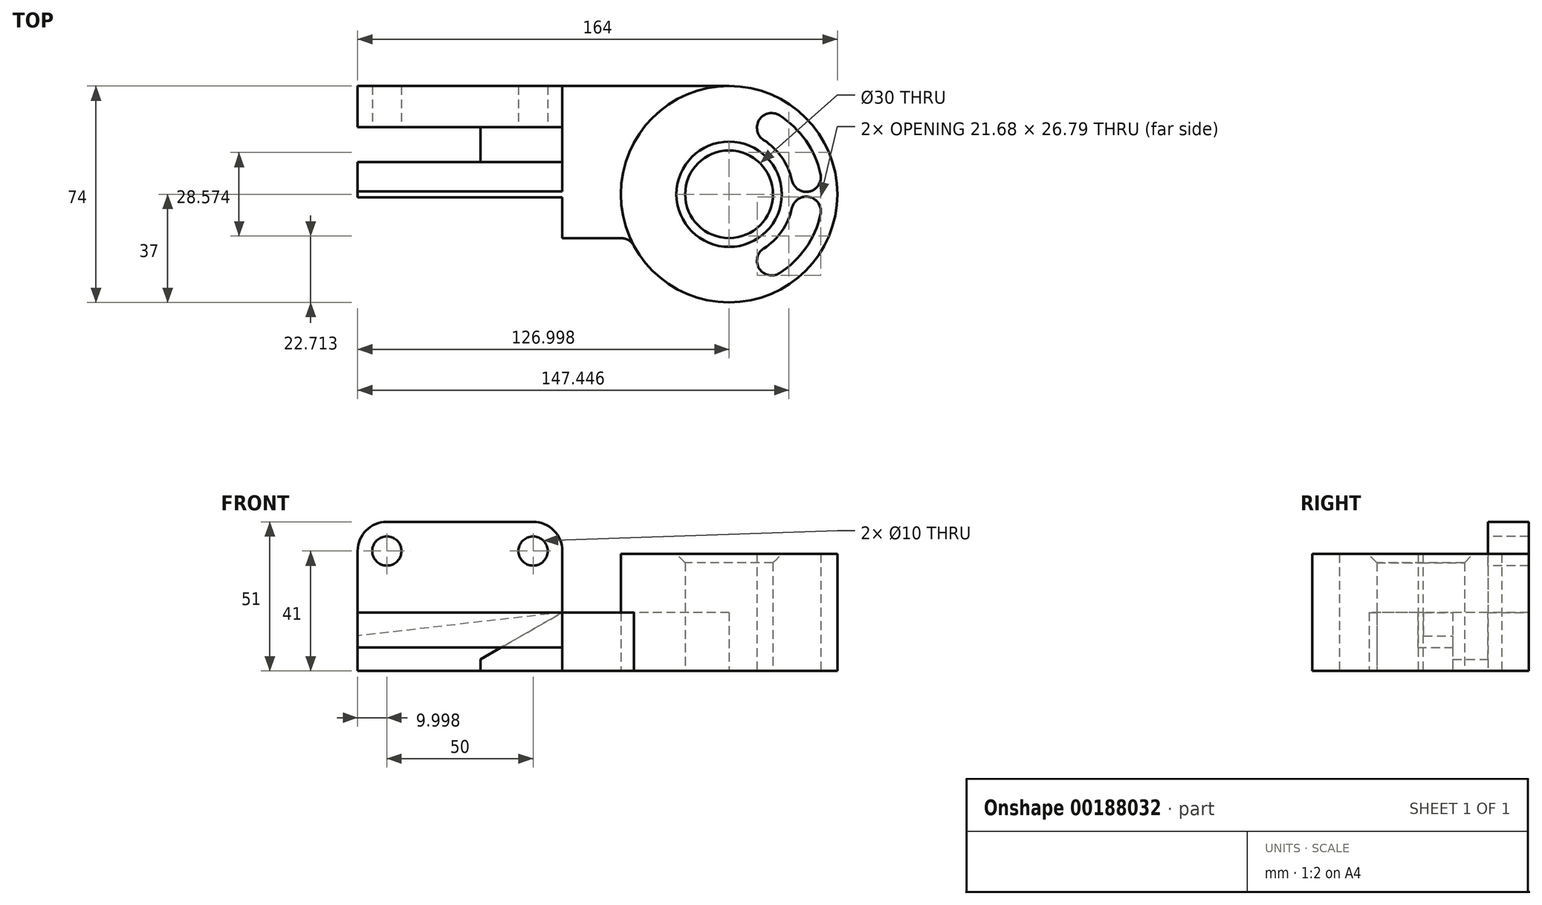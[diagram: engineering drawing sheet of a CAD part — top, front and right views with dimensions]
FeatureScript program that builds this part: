
annotation { "Feature Type Name" : "Feature", "Feature Type Description" : "" }
export const myFeature = defineFeature(function(context is Context, id is Id, definition is map)
    precondition{}
    {
        {
            var Q0;
            Q0=qCreatedBy(makeId("Top.planeOp"),FACE);
            var sketch = newSketch(context, id + "F0", { "sketchPlane" : qUnion([Q0])});
            skCircle(sketch, "E0", {"center": v(50.74, 37) * mm, "radius": 37 * mm});
            skArc(sketch, "E1", {"start": v(67.96, 10.03) * mm, "mid": v(76.97, 18.67) * mm, "end": v(81.99, 30.1) * mm});
            skCircle(sketch, "E2", {"center": v(50.74, 37) * mm, "radius": 22 * mm});
            skCircle(sketch, "E3", {"center": v(50.74, 37) * mm, "radius": 15 * mm});
            skArc(sketch, "E4", {"start": v(81.99, 30.1) * mm, "mid": v(78.18, 36.07) * mm, "end": v(72.22, 32.26) * mm});
            skArc(sketch, "E5", {"start": v(62.58, 18.46) * mm, "mid": v(61.05, 11.55) * mm, "end": v(67.96, 10.03) * mm});
            skArc(sketch, "E6.MirrorCS", {"start": v(81.99, 43.9) * mm, "mid": v(78.18, 37.93) * mm, "end": v(72.22, 41.74) * mm});
            skArc(sketch, "E7.MirrorCS", {"start": v(62.58, 55.54) * mm, "mid": v(61.05, 62.45) * mm, "end": v(67.96, 63.97) * mm});
            skLineSegment(sketch, "E8", {"start": v(50.74, 74) * mm, "end": v(-76.26, 74) * mm});
            skLineSegment(sketch, "E9", {"start": v(-76.26, 74) * mm, "end": v(-76.26, 22) * mm});
            skLineSegment(sketch, "E10", {"start": v(-76.26, 22) * mm, "end": v(13.8, 22) * mm});
            skArc(sketch, "E11", {"start": v(18.2, 19.38) * mm, "mid": v(16.36, 21.3) * mm, "end": v(13.8, 22) * mm});
            skArc(sketch, "E12.trimOffspring", {"start": v(81.99, 43.9) * mm, "mid": v(76.97, 55.33) * mm, "end": v(67.96, 63.97) * mm});
            skPoint(sketch, "E13", {"position": v(-76.26, 48) * mm});
            skLineSegment(sketch, "E14", {"start": v(-76.26, 22) * mm, "end": v(-12.4, 22) * mm});
            skLineSegment(sketch, "E15", {"start": v(-6.26, 74) * mm, "end": v(-6.26, 22) * mm});
            skLineSegment(sketch, "E16", {"start": v(-76.26, 36) * mm, "end": v(-6.26, 36) * mm});
            skLineSegment(sketch, "E17", {"start": v(-76.26, 60) * mm, "end": v(-6.26, 60) * mm});
            skLineSegment(sketch, "E18", {"start": v(-76.26, 48) * mm, "end": v(-6.26, 48) * mm});
            skLineSegment(sketch, "E19", {"start": v(-34.26, 60) * mm, "end": v(-34.26, 48) * mm});
            skSolve(sketch);
        }
        {
            var Q0;
            Q0=makeQuery(id+"F0.imprint","IMPRINT",FACE,{"disambiguationData":[TD([[makeQuery(id+"F0.imprint","IMPRINT",EDGE,{"derivedFrom":sQuery(id+"F0.wireOp",EDGE,"E1")}),-1.0]])]});
            var Q1;
            Q1=makeQuery(id+"F0.imprint","IMPRINT",FACE,{"disambiguationData":[TD([[makeQuery(id+"F0.imprint","IMPRINT",EDGE,{"derivedFrom":sQuery(id+"F0.wireOp",EDGE,"VI8LkTya-be0w-nu0Q-2iVm-8yqCSl8gfKjl")}),-1.0]])]});
            var Q2;
            Q2=makeQuery(id+"F0.imprint","IMPRINT",FACE,{"disambiguationData":[TD([[makeQuery(id+"F0.imprint","IMPRINT",EDGE,{"derivedFrom":sQuery(id+"F0.wireOp",EDGE,"E3")}),-1.0]])]});
            extrude(context, id + "F1", {"entities" : qUnion([Q0, Q1, Q2]), "depth" : 40 * mm});
        }
        {
            var Q0;
            {var subQ0=sQuery(id+"F0.wireOp",EDGE,"E11");Q0=makeQuery(id+"F0.imprint","IMPRINT",FACE,{"disambiguationData":[TD([[makeQuery(id+"F0.imprint","IMPRINT",EDGE,{"derivedFrom":subQ0}),-1.0]])]});}
            var Q1;
            {var subQ4=sQuery(id+"F0.wireOp",EDGE,"E14");Q1=makeQuery(id+"F0.imprint","IMPRINT",FACE,{"disambiguationData":[TD([[makeQuery(id+"F0.imprint","IMPRINT",EDGE,{"derivedFrom":subQ4}),1.0]])]});}
            var Q2;
            {var subQ0=sQuery(id+"F0.wireOp",EDGE,"E16");Q2=makeQuery(id+"F0.imprint","IMPRINT",FACE,{"disambiguationData":[TD([[makeQuery(id+"F0.imprint","IMPRINT",EDGE,{"derivedFrom":subQ0}),1.0]])]});}
            var Q3;
            {var subQ5=sQuery(id+"F0.wireOp",EDGE,"E17");Q3=makeQuery(id+"F0.imprint","IMPRINT",FACE,{"disambiguationData":[TD([[makeQuery(id+"F0.imprint","IMPRINT",EDGE,{"derivedFrom":subQ5}),1.0]])]});}
            extrude(context, id + "F2", {"entities" : qUnion([Q0, Q1, Q2, Q3]), "depth" : 20 * mm});
        }
        {
            var Q0;
            Q0=makeQuery(id+"F2.opExtrude","SWEPT_FACE",FACE,{"disambiguationData":[OSD([sQuery(id+"F0.wireOp",EDGE,"E18")])]});
            var sketch = newSketch(context, id + "F3", { "sketchPlane" : qUnion([Q0])});
            skLineSegment(sketch, "E20", {"start": v(76.26, 20) * mm, "end": v(76.26, 12) * mm});
            skLineSegment(sketch, "E21", {"start": v(76.26, 0) * mm, "end": v(76.26, 8) * mm});
            skLineSegment(sketch, "E22", {"start": v(76.26, 12) * mm, "end": v(76.26, 8) * mm});
            skLineSegment(sketch, "E23", {"start": v(76.26, 20) * mm, "end": v(6.26, 20) * mm});
            skLineSegment(sketch, "E24", {"start": v(6.26, 20) * mm, "end": v(6.26, 0) * mm});
            skLineSegment(sketch, "E25", {"start": v(76.26, 20) * mm, "end": v(76.26, 0) * mm});
            skLineSegment(sketch, "E26", {"start": v(6.26, 20) * mm, "end": v(76.26, 12) * mm});
            skLineSegment(sketch, "E27", {"start": v(76.26, 8) * mm, "end": v(76.26, 12) * mm});
            skLineSegment(sketch, "E28", {"start": v(76.26, 8) * mm, "end": v(6.26, 8) * mm});
            skLineSegment(sketch, "E29", {"start": v(6.26, 0) * mm, "end": v(76.26, 0) * mm});
            skSolve(sketch);
        }
        {
            var Q0;
            {var subQ0=sQuery(id+"F3.wireOp",EDGE,"E23");Q0=makeQuery(id+"F3.imprint","IMPRINT",FACE,{"disambiguationData":[TD([[makeQuery(id+"F3.imprint","IMPRINT",EDGE,{"derivedFrom":subQ0}),1.0]])]});}
            extrude(context, id + "F4", {"entities" : qUnion([Q0]), "operationType" : NewBodyOperationType.REMOVE, "oppositeDirection" : true, "depth" : 10 * mm});
        }
        {
            var Q0;
            {var subQ2=sQuery(id+"F3.wireOp",EDGE,"E28");Q0=makeQuery(id+"F3.imprint","IMPRINT",FACE,{"disambiguationData":[TD([[makeQuery(id+"F3.imprint","IMPRINT",EDGE,{"derivedFrom":subQ2}),1.0]])]});}
            extrude(context, id + "F5", {"entities" : qUnion([Q0]), "operationType" : NewBodyOperationType.REMOVE, "oppositeDirection" : true, "depth" : 12 * mm});
        }
        {
            var Q0;
            Q0=makeQuery(id+"F2.opExtrude","CAP_FACE",FACE,{"disambiguationData":[OSD([sQuery(id+"F0.wireOp",EDGE,"E0"),sQuery(id+"F0.wireOp",EDGE,"E8"),sQuery(id+"F0.wireOp",EDGE,"E9"),sQuery(id+"F0.wireOp",EDGE,"E10"),sQuery(id+"F0.wireOp",EDGE,"E11"),sQuery(id+"F0.wireOp",EDGE,"E14"),sQuery(id+"F0.wireOp",EDGE,"E15"),sQuery(id+"F0.wireOp",EDGE,"E17"),sQuery(id+"F0.wireOp",EDGE,"E18")])],"isStart":false});
            var sketch = newSketch(context, id + "F6", { "sketchPlane" : qUnion([Q0])});
            skLineSegment(sketch, "E30", {"start": v(-6.26, 60) * mm, "end": v(-6.26, 74) * mm});
            skPoint(sketch, "E30.endSnap0", {"position": v(-12.76, 74) * mm});
            skSolve(sketch);
        }
        {
            var Q0;
            {var subQ0=sQuery(id+"F6.wireOp",EDGE,"E30");Q0=makeQuery(id+"F6.imprint","IMPRINT",FACE,{"disambiguationData":[TD([[makeQuery(id+"F6.imprint","IMPRINT",EDGE,{"derivedFrom":subQ0}),1.0]])]});}
            extrude(context, id + "F7", {"entities" : qUnion([Q0]), "operationType" : NewBodyOperationType.ADD, "depth" : 31 * mm});
        }
        {
            var Q0;
            {var subQ0=sQuery(id+"F0.wireOp",EDGE,"E17");Q0=makeQuery(id+"F7.boolean.opBoolean","MERGE",FACE,{"derivedFrom":[makeQuery(id+"F2.opExtrude","SWEPT_FACE",FACE,{"disambiguationData":[OSD([subQ0])]}),makeQuery(id+"F7.opExtrude","SWEPT_FACE",FACE,{"disambiguationData":[OSD([subQ0])]})]});}
            var sketch = newSketch(context, id + "F8", { "sketchPlane" : qUnion([Q0])});
            skLineSegment(sketch, "E31", {"start": v(-6.26, 51) * mm, "end": v(-16.26, 51) * mm});
            skLineSegment(sketch, "E32", {"start": v(-76.26, 51) * mm, "end": v(-66.26, 51) * mm});
            skLineSegment(sketch, "E33", {"start": v(-66.26, 51) * mm, "end": v(-66.26, 41) * mm});
            skLineSegment(sketch, "E34", {"start": v(-16.26, 51) * mm, "end": v(-16.26, 41) * mm});
            skCircle(sketch, "E35", {"center": v(-66.26, 41) * mm, "radius": 5 * mm});
            skCircle(sketch, "E36", {"center": v(-16.26, 41) * mm, "radius": 5 * mm});
            skCircle(sketch, "E37", {"center": v(-66.26, 41) * mm, "radius": 10 * mm});
            skCircle(sketch, "E38", {"center": v(-16.26, 41) * mm, "radius": 10 * mm});
            skSolve(sketch);
        }
        {
            var Q0;
            Q0=makeQuery(id+"F8.imprint","IMPRINT",FACE,{"disambiguationData":[TD([[makeQuery(id+"F8.imprint","IMPRINT",EDGE,{"derivedFrom":sQuery(id+"F8.wireOp",EDGE,"E35")}),1.0]])]});
            var Q1;
            {var subQ0=sQuery(id+"F8.wireOp",EDGE,"E32");Q1=makeQuery(id+"F8.imprint","IMPRINT",FACE,{"disambiguationData":[TD([[makeQuery(id+"F8.imprint","IMPRINT",EDGE,{"derivedFrom":subQ0}),-1.0]])]});}
            var Q2;
            {var subQ0=sQuery(id+"F8.wireOp",EDGE,"E31");Q2=makeQuery(id+"F8.imprint","IMPRINT",FACE,{"disambiguationData":[TD([[makeQuery(id+"F8.imprint","IMPRINT",EDGE,{"derivedFrom":subQ0}),-1.0]])]});}
            var Q3;
            Q3=makeQuery(id+"F8.imprint","IMPRINT",FACE,{"disambiguationData":[TD([[makeQuery(id+"F8.imprint","IMPRINT",EDGE,{"derivedFrom":sQuery(id+"F8.wireOp",EDGE,"E36")}),1.0]])]});
            extrude(context, id + "F9", {"entities" : qUnion([Q0, Q1, Q2, Q3]), "operationType" : NewBodyOperationType.REMOVE, "endBound" : BoundingType.THROUGH_ALL, "oppositeDirection" : true, "depth" : 25 * mm});
        }
        {
            var Q0;
            {var subQ5=sQuery(id+"F0.wireOp",EDGE,"E19");Q0=makeQuery(id+"F0.imprint","IMPRINT",FACE,{"disambiguationData":[TD([[makeQuery(id+"F0.imprint","IMPRINT",EDGE,{"derivedFrom":subQ5}),1.0]])]});}
            extrude(context, id + "F10", {"entities" : qUnion([Q0]), "operationType" : NewBodyOperationType.ADD, "depth" : 20 * mm});
        }
        {
            var Q0;
            Q0=makeQuery(id+"F10.opExtrude","CAP_EDGE",EDGE,{"disambiguationData":[OSD([sQuery(id+"F0.wireOp",EDGE,"E19")])],"isStart":false});
            chamfer(context, id + "F11", {"entities" : qUnion([Q0]), "chamferType" : ChamferType.TWO_OFFSETS, "width1" : 28 * mm, "oppositeDirection" : false, "width2" : 16 * mm, "tangentPropagation" : true});
        }
        {
            var Q0;
            Q0=makeQuery(id+"F1.opExtrude","CAP_EDGE",EDGE,{"disambiguationData":[OSD([sQuery(id+"F0.wireOp",EDGE,"E3")])],"isStart":false});
            chamfer(context, id + "F12", {"entities" : qUnion([Q0]), "width" : 3 * mm, "tangentPropagation" : true});
        }
    });
